# Revit family: Elate LED Desk Lamp
name_source: partatom
category: Lighting Fixtures
revit_build: Autodesk Revit 2018 (Build: 20190510_1515(x64)
units: mm (PartAtom-declared; Revit-internal decimal feet)

## family parameters
Cut with Voids When Loaded = No
Host = Face
Light Source = Yes
OmniClass Number = 23.80.70.11.11
OmniClass Title = General Luminaries, Non Directional
Part Type = Normal
Room Calculation Point = No
Round Connector Dimension = Use Diameter
Shared = No

## types (4) — shared parameters
Ballast Number of Poles = 1
Color Filter = 16777215
Default Elevation = 4' - 0"
Dimming Lamp Color Temperature Shift = <None>
Emit Shape Visible in Rendering = No
Lamp = T-12
Load Classification = Lighting - Dwelling Unit

## per-type parameters (varying)
| type | Apparent Load | Ballast Voltage | Emit from Circle Diameter | Finish | Light Source Symbol Size |
| 48" - 120V | 40 VA | 120 V | 0' - 2" | Elate Desk Lamp White | 0' - 4" |
| 48" - 277V | 40 VA | 277 V | 2' - 0" | <By Category> | 2' - 0" |
| 96" - 120V | 64 VA | 120 V | 2' - 0" | <By Category> | 2' - 0" |
| 96" - 277V | 64 VA | 277 V | 2' - 0" | <By Category> | 2' - 0" |

## geometry (parser evidence)
native form markers: Sweep x2
no freeform markers — native parametric forms only
